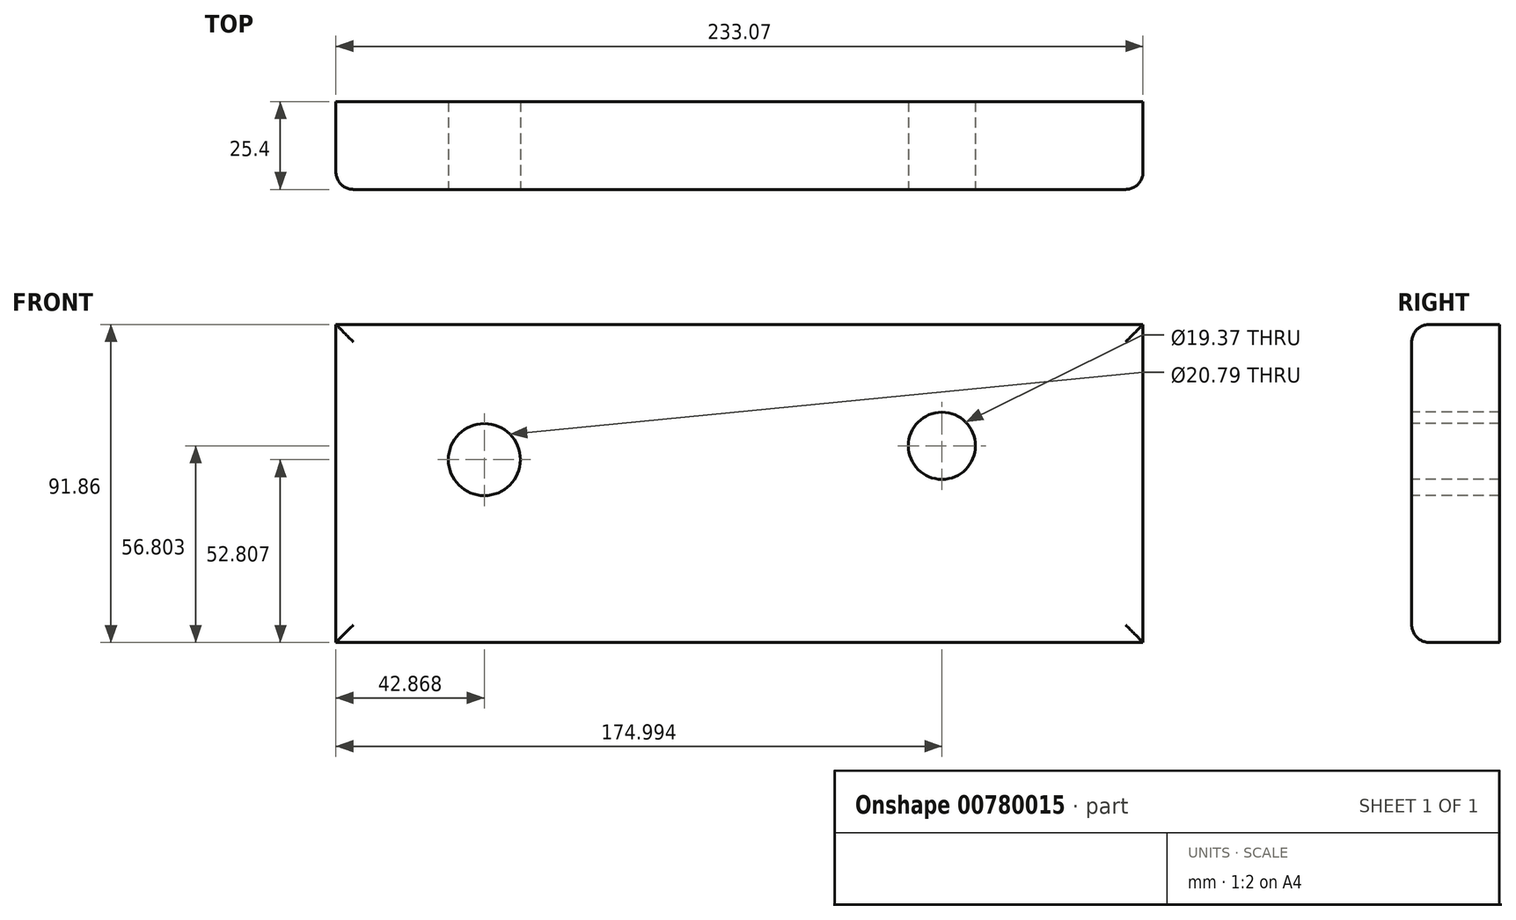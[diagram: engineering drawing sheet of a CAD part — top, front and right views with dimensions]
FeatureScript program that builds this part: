
annotation { "Feature Type Name" : "Feature", "Feature Type Description" : "" }
export const myFeature = defineFeature(function(context is Context, id is Id, definition is map)
    precondition{}
    {
        {
            var Q0;
            Q0=qCreatedBy(makeId("Front.planeOp"),FACE);
            var sketch = newSketch(context, id + "F0", { "sketchPlane" : qUnion([Q0])});
            skLineSegment(sketch, "E0.bottom", {"start": v(-115.05, 53.63) * mm, "end": v(118.02, 53.63) * mm});
            skLineSegment(sketch, "E0.top", {"start": v(-115.05, -38.23) * mm, "end": v(118.02, -38.23) * mm});
            skLineSegment(sketch, "E0.left", {"start": v(-115.05, 53.63) * mm, "end": v(-115.05, -38.23) * mm});
            skLineSegment(sketch, "E0.right", {"start": v(118.02, 53.63) * mm, "end": v(118.02, -38.23) * mm});
            skSolve(sketch);
        }
        {
            var Q0;
            Q0 = qSketchRegion(id + "F0", true);
            extrude(context, id + "F1", {"entities" : qUnion([Q0]), "depth" : 25.4 * mm, "offsetDistance" : 25.4 * mm});
        }
        {
            var Q0;
            Q0=makeQuery(id+"F1.opExtrude","CAP_FACE",FACE,{"disambiguationData":[OSD([sQuery(id+"F0.wireOp",EDGE,"E0.bottom"),sQuery(id+"F0.wireOp",EDGE,"E0.top"),sQuery(id+"F0.wireOp",EDGE,"E0.left"),sQuery(id+"F0.wireOp",EDGE,"E0.right")])],"isStart":false});
            fillet(context, id + "F2", {"entities" : qUnion([Q0]), "radius" : 5.08 * mm, "tangentPropagation" : true, "allowEdgeOverflow" : false});
        }
        {
            var Q0;
            Q0=makeQuery(id+"F1.opExtrude","CAP_FACE",FACE,{"disambiguationData":[OSD([sQuery(id+"F0.wireOp",EDGE,"E0.bottom"),sQuery(id+"F0.wireOp",EDGE,"E0.top"),sQuery(id+"F0.wireOp",EDGE,"E0.left"),sQuery(id+"F0.wireOp",EDGE,"E0.right")])],"isStart":false});
            var sketch = newSketch(context, id + "F3", { "sketchPlane" : qUnion([Q0])});
            skCircle(sketch, "E1", {"center": v(-72.18, 14.58) * mm, "radius": 10.4 * mm});
            skCircle(sketch, "E2", {"center": v(59.94, 18.57) * mm, "radius": 9.69 * mm});
            skSolve(sketch);
        }
        {
            var Q0;
            Q0 = qSketchRegion(id + "F3", true);
            extrude(context, id + "F4", {"entities" : qUnion([Q0]), "operationType" : NewBodyOperationType.REMOVE, "oppositeDirection" : true, "depth" : 25.4 * mm, "offsetDistance" : 25.4 * mm});
        }
    });
